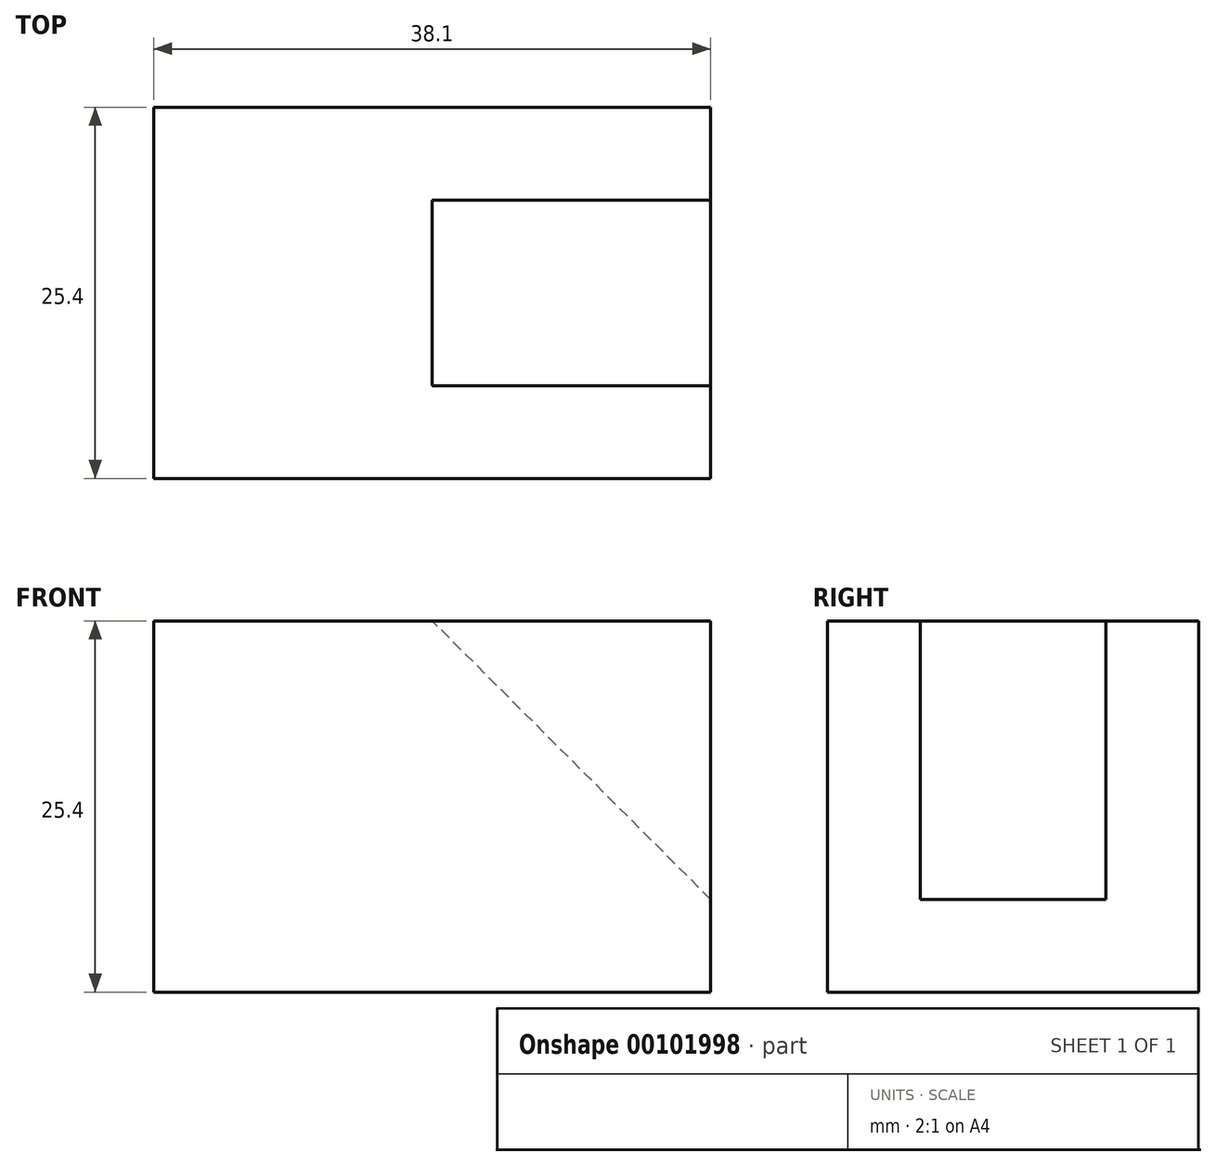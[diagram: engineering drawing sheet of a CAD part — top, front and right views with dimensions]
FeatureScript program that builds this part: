
annotation { "Feature Type Name" : "Feature", "Feature Type Description" : "" }
export const myFeature = defineFeature(function(context is Context, id is Id, definition is map)
    precondition{}
    {
        {
            var Q0;
            Q0=qCreatedBy(makeId("Front.planeOp"),FACE);
            var sketch = newSketch(context, id + "F0", { "sketchPlane" : qUnion([Q0])});
            skLineSegment(sketch, "E0", {"start": v(0, 0) * mm, "end": v(0, 25.4) * mm});
            skLineSegment(sketch, "E1", {"start": v(0, 25.4) * mm, "end": v(38.1, 25.4) * mm});
            skLineSegment(sketch, "E2", {"start": v(38.1, 25.4) * mm, "end": v(38.1, 0) * mm});
            skLineSegment(sketch, "E3", {"start": v(38.1, 0) * mm, "end": v(0, 0) * mm});
            skSolve(sketch);
        }
        {
            var Q0;
            Q0 = qSketchRegion(id + "F0", true);
            extrude(context, id + "F1", {"entities" : qUnion([Q0]), "depth" : 25.4 * mm});
        }
        {
            var Q0;
            Q0=qCreatedBy(makeId("Front.planeOp"),FACE);
            var sketch = newSketch(context, id + "F2", { "sketchPlane" : qUnion([Q0])});
            skLineSegment(sketch, "E4", {"start": v(38.1, 6.35) * mm, "end": v(19.05, 25.4) * mm});
            skLineSegment(sketch, "E5", {"start": v(19.05, 25.4) * mm, "end": v(38.1, 25.4) * mm});
            skLineSegment(sketch, "E6", {"start": v(38.1, 25.4) * mm, "end": v(38.1, 6.35) * mm});
            skSolve(sketch);
        }
        {
            var Q0;
            Q0=makeQuery(id+"F2.imprint","IMPRINT",FACE,{"disambiguationData":[TD([[makeQuery(id+"F2.imprint","IMPRINT",EDGE,{"derivedFrom":sQuery(id+"F2.wireOp",EDGE,"E4")}),-1.0]])]});
            extrude(context, id + "F3", {"entities" : qUnion([Q0]), "operationType" : NewBodyOperationType.REMOVE, "depth" : 19.05 * mm, "hasSecondDirection" : true, "secondDirectionOppositeDirection" : false, "secondDirectionDepth" : 6.35 * mm});
        }
    });
